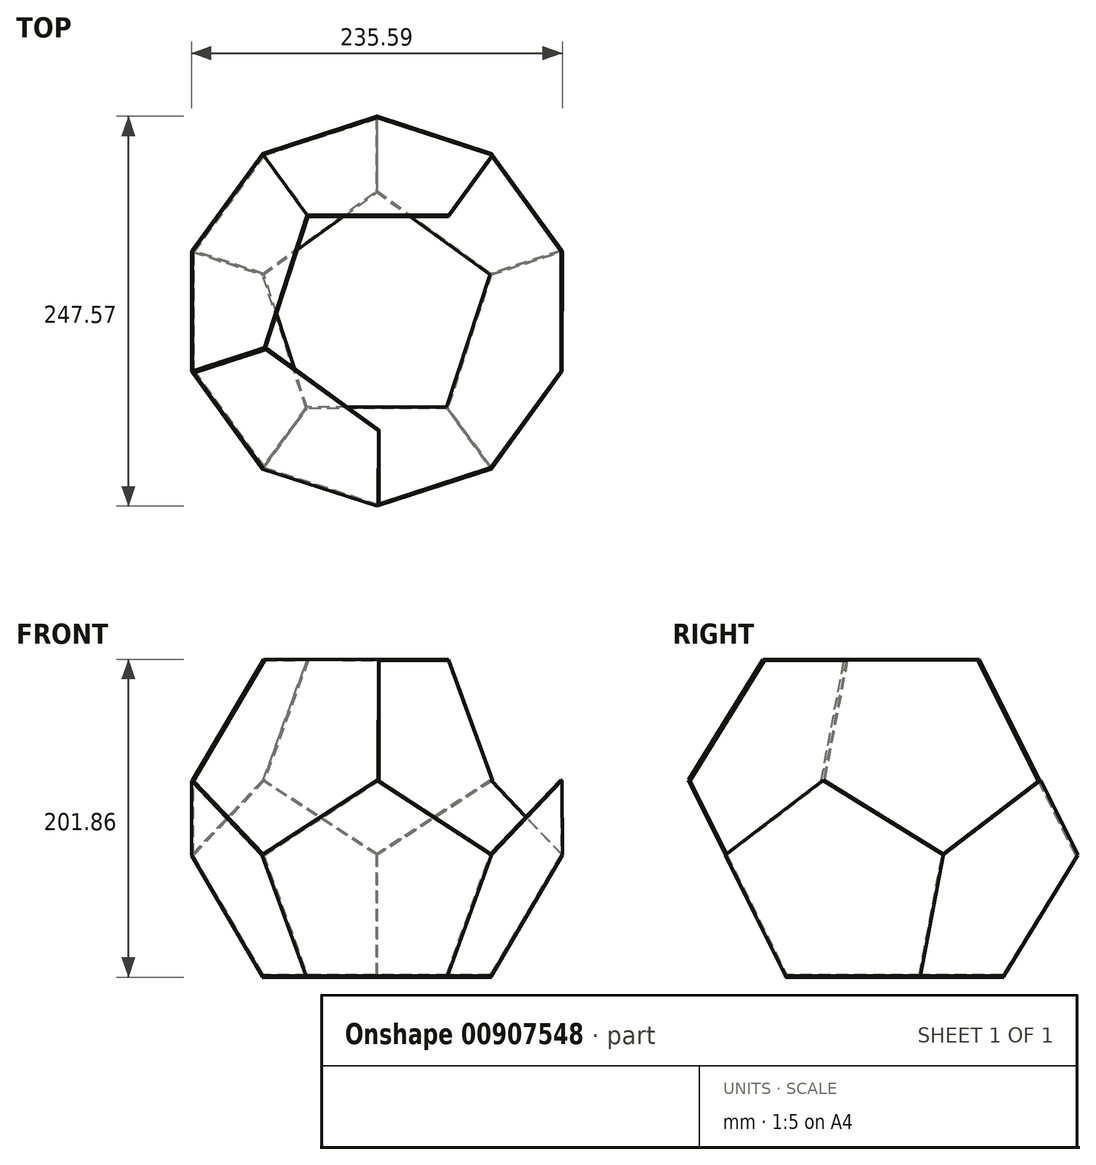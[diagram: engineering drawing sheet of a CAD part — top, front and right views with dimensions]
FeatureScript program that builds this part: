
annotation { "Feature Type Name" : "Feature", "Feature Type Description" : "" }
export const myFeature = defineFeature(function(context is Context, id is Id, definition is map)
    precondition{}
    {
        {
            var Q0;
            Q0=qCreatedBy(makeId("Top.planeOp"),FACE);
            var sketch = newSketch(context, id + "F0", { "sketchPlane" : qUnion([Q0])});
            skCircle(sketch, "E0.cCircle", {"center": v(0, 0) * mm, "radius": 61.94 * mm, "construction": true});
            skLineSegment(sketch, "E0.0", {"start": v(72.81, 23.66) * mm, "end": v(45, -61.94) * mm});
            skLineSegment(sketch, "E0.1", {"start": v(45, -61.94) * mm, "end": v(-45, -61.94) * mm});
            skLineSegment(sketch, "E0.2", {"start": v(-45, -61.94) * mm, "end": v(-72.81, 23.66) * mm});
            skLineSegment(sketch, "E0.3", {"start": v(-72.81, 23.66) * mm, "end": v(0, 76.56) * mm});
            skLineSegment(sketch, "E0.4", {"start": v(0, 76.56) * mm, "end": v(72.81, 23.66) * mm});
            skPoint(sketch, "E0.0.midPoint", {"position": v(58.9, -19.14) * mm});
            skSolve(sketch);
        }
        {
            var Q0;
            Q0=makeQuery(id+"F0.imprint","IMPRINT",FACE,{"disambiguationData":[TD([[makeQuery(id+"F0.imprint","IMPRINT",EDGE,{"derivedFrom":sQuery(id+"F0.wireOp",EDGE,"E0.0")}),-1.0]])]});
            extrude(context, id + "F1", {"entities" : qUnion([Q0]), "depth" : 1 * mm, "offsetDistance" : 25 * mm});
        }
        {
            var Q0;
            Q0=makeQuery(id+"F1.opExtrude","SWEPT_BODY",BODY,{"disambiguationData":[OSD([sQuery(id+"F0.wireOp",EDGE,"E0.0"),sQuery(id+"F0.wireOp",EDGE,"E0.1"),sQuery(id+"F0.wireOp",EDGE,"E0.2"),sQuery(id+"F0.wireOp",EDGE,"E0.3"),sQuery(id+"F0.wireOp",EDGE,"E0.4")])]});
            transform(context, id + "F2", {"entities" : qUnion([Q0]), "transformType" : TransformType.COPY});
        }
        {
            var Q0;
            Q0=makeQuery(id+"F2.opPattern","COPY",BODY,{"derivedFrom":makeQuery(id+"F1.opExtrude","SWEPT_BODY",BODY,{"disambiguationData":[OSD([sQuery(id+"F0.wireOp",EDGE,"E0.0"),sQuery(id+"F0.wireOp",EDGE,"E0.1"),sQuery(id+"F0.wireOp",EDGE,"E0.2"),sQuery(id+"F0.wireOp",EDGE,"E0.3"),sQuery(id+"F0.wireOp",EDGE,"E0.4")])]}),"instanceName":"1"});
            var Q1;
            Q1=makeQuery(id+"F1.opExtrude","CAP_EDGE",EDGE,{"disambiguationData":[OSD([sQuery(id+"F0.wireOp",EDGE,"E0.2")])],"isStart":false});
            transform(context, id + "F3", {"entities" : qUnion([Q0]), "transformType" : TransformType.ROTATION, "transformAxis" : qUnion([Q1]), "angle" : 116.57 * degree, "oppositeDirection" : true, "makeCopy" : false});
        }
        {
            var Q0;
            Q0=makeQuery(id+"F1.opExtrude","SWEPT_BODY",BODY,{"disambiguationData":[OSD([sQuery(id+"F0.wireOp",EDGE,"E0.0"),sQuery(id+"F0.wireOp",EDGE,"E0.1"),sQuery(id+"F0.wireOp",EDGE,"E0.2"),sQuery(id+"F0.wireOp",EDGE,"E0.3"),sQuery(id+"F0.wireOp",EDGE,"E0.4")])]});
            transform(context, id + "F4", {"entities" : qUnion([Q0]), "transformType" : TransformType.COPY});
        }
        {
            var Q0;
            Q0=makeQuery(id+"F4.opPattern","COPY",BODY,{"derivedFrom":makeQuery(id+"F1.opExtrude","SWEPT_BODY",BODY,{"disambiguationData":[OSD([sQuery(id+"F0.wireOp",EDGE,"E0.0"),sQuery(id+"F0.wireOp",EDGE,"E0.1"),sQuery(id+"F0.wireOp",EDGE,"E0.2"),sQuery(id+"F0.wireOp",EDGE,"E0.3"),sQuery(id+"F0.wireOp",EDGE,"E0.4")])]}),"instanceName":"1"});
            var Q1;
            Q1=makeQuery(id+"F1.opExtrude","CAP_EDGE",EDGE,{"disambiguationData":[OSD([sQuery(id+"F0.wireOp",EDGE,"E0.3")])],"isStart":false});
            transform(context, id + "F5", {"entities" : qUnion([Q0]), "transformType" : TransformType.ROTATION, "transformAxis" : qUnion([Q1]), "angle" : 116.51 * degree, "oppositeDirection" : true, "makeCopy" : false});
        }
        {
            var Q0;
            Q0=makeQuery(id+"F1.opExtrude","SWEPT_BODY",BODY,{"disambiguationData":[OSD([sQuery(id+"F0.wireOp",EDGE,"E0.0"),sQuery(id+"F0.wireOp",EDGE,"E0.1"),sQuery(id+"F0.wireOp",EDGE,"E0.2"),sQuery(id+"F0.wireOp",EDGE,"E0.3"),sQuery(id+"F0.wireOp",EDGE,"E0.4")])]});
            transform(context, id + "F6", {"entities" : qUnion([Q0]), "transformType" : TransformType.COPY});
        }
        {
            var Q0;
            Q0=makeQuery(id+"F6.opPattern","COPY",BODY,{"derivedFrom":makeQuery(id+"F1.opExtrude","SWEPT_BODY",BODY,{"disambiguationData":[OSD([sQuery(id+"F0.wireOp",EDGE,"E0.0"),sQuery(id+"F0.wireOp",EDGE,"E0.1"),sQuery(id+"F0.wireOp",EDGE,"E0.2"),sQuery(id+"F0.wireOp",EDGE,"E0.3"),sQuery(id+"F0.wireOp",EDGE,"E0.4")])]}),"instanceName":"1"});
            var Q1;
            Q1=makeQuery(id+"F1.opExtrude","CAP_EDGE",EDGE,{"disambiguationData":[OSD([sQuery(id+"F0.wireOp",EDGE,"E0.4")])],"isStart":false});
            transform(context, id + "F7", {"entities" : qUnion([Q0]), "transformType" : TransformType.ROTATION, "transformAxis" : qUnion([Q1]), "angle" : 116.51 * degree, "oppositeDirection" : true, "makeCopy" : false});
        }
        {
            var Q0;
            Q0=makeQuery(id+"F1.opExtrude","SWEPT_BODY",BODY,{"disambiguationData":[OSD([sQuery(id+"F0.wireOp",EDGE,"E0.0"),sQuery(id+"F0.wireOp",EDGE,"E0.1"),sQuery(id+"F0.wireOp",EDGE,"E0.2"),sQuery(id+"F0.wireOp",EDGE,"E0.3"),sQuery(id+"F0.wireOp",EDGE,"E0.4")])]});
            transform(context, id + "F8", {"entities" : qUnion([Q0]), "transformType" : TransformType.COPY});
        }
        {
            var Q0;
            Q0=makeQuery(id+"F8.opPattern","COPY",BODY,{"derivedFrom":makeQuery(id+"F1.opExtrude","SWEPT_BODY",BODY,{"disambiguationData":[OSD([sQuery(id+"F0.wireOp",EDGE,"E0.0"),sQuery(id+"F0.wireOp",EDGE,"E0.1"),sQuery(id+"F0.wireOp",EDGE,"E0.2"),sQuery(id+"F0.wireOp",EDGE,"E0.3"),sQuery(id+"F0.wireOp",EDGE,"E0.4")])]}),"instanceName":"1"});
            var Q1;
            Q1=makeQuery(id+"F1.opExtrude","CAP_EDGE",EDGE,{"disambiguationData":[OSD([sQuery(id+"F0.wireOp",EDGE,"E0.0")])],"isStart":false});
            transform(context, id + "F9", {"entities" : qUnion([Q0]), "transformType" : TransformType.ROTATION, "transformAxis" : qUnion([Q1]), "angle" : 116.51 * degree, "oppositeDirection" : true, "makeCopy" : false});
        }
        {
            var Q0;
            Q0=makeQuery(id+"F1.opExtrude","SWEPT_BODY",BODY,{"disambiguationData":[OSD([sQuery(id+"F0.wireOp",EDGE,"E0.0"),sQuery(id+"F0.wireOp",EDGE,"E0.1"),sQuery(id+"F0.wireOp",EDGE,"E0.2"),sQuery(id+"F0.wireOp",EDGE,"E0.3"),sQuery(id+"F0.wireOp",EDGE,"E0.4")])]});
            transform(context, id + "F10", {"entities" : qUnion([Q0]), "transformType" : TransformType.COPY});
        }
        {
            var Q0;
            Q0=makeQuery(id+"F10.opPattern","COPY",BODY,{"derivedFrom":makeQuery(id+"F1.opExtrude","SWEPT_BODY",BODY,{"disambiguationData":[OSD([sQuery(id+"F0.wireOp",EDGE,"E0.0"),sQuery(id+"F0.wireOp",EDGE,"E0.1"),sQuery(id+"F0.wireOp",EDGE,"E0.2"),sQuery(id+"F0.wireOp",EDGE,"E0.3"),sQuery(id+"F0.wireOp",EDGE,"E0.4")])]}),"instanceName":"1"});
            var Q1;
            Q1=makeQuery(id+"F1.opExtrude","CAP_EDGE",EDGE,{"disambiguationData":[OSD([sQuery(id+"F0.wireOp",EDGE,"E0.1")])],"isStart":false});
            transform(context, id + "F11", {"entities" : qUnion([Q0]), "transformType" : TransformType.ROTATION, "transformAxis" : qUnion([Q1]), "angle" : 116.51 * degree, "oppositeDirection" : true, "makeCopy" : false});
        }
        {
            var Q0;
            Q0=makeQuery(id+"F4.opPattern","COPY",BODY,{"derivedFrom":makeQuery(id+"F1.opExtrude","SWEPT_BODY",BODY,{"disambiguationData":[OSD([sQuery(id+"F0.wireOp",EDGE,"E0.0"),sQuery(id+"F0.wireOp",EDGE,"E0.1"),sQuery(id+"F0.wireOp",EDGE,"E0.2"),sQuery(id+"F0.wireOp",EDGE,"E0.3"),sQuery(id+"F0.wireOp",EDGE,"E0.4")])]}),"instanceName":"1"});
            transform(context, id + "F12", {"entities" : qUnion([Q0]), "transformType" : TransformType.COPY});
        }
        {
            var Q0;
            Q0=makeQuery(id+"F12.opPattern","COPY",BODY,{"derivedFrom":makeQuery(id+"F4.opPattern","COPY",BODY,{"derivedFrom":makeQuery(id+"F1.opExtrude","SWEPT_BODY",BODY,{"disambiguationData":[OSD([sQuery(id+"F0.wireOp",EDGE,"E0.0"),sQuery(id+"F0.wireOp",EDGE,"E0.1"),sQuery(id+"F0.wireOp",EDGE,"E0.2"),sQuery(id+"F0.wireOp",EDGE,"E0.3"),sQuery(id+"F0.wireOp",EDGE,"E0.4")])]}),"instanceName":"1"}),"instanceName":"1"});
            var Q1;
            Q1=makeQuery(id+"F4.opPattern","COPY",EDGE,{"derivedFrom":makeQuery(id+"F1.opExtrude","CAP_EDGE",EDGE,{"disambiguationData":[OSD([sQuery(id+"F0.wireOp",EDGE,"E0.0")])],"isStart":true}),"instanceName":"1"});
            transform(context, id + "F13", {"entities" : qUnion([Q0]), "transformType" : TransformType.ROTATION, "transformAxis" : qUnion([Q1]), "angle" : 116.51 * degree, "makeCopy" : false});
        }
        {
            var Q0;
            Q0=makeQuery(id+"F12.opPattern","COPY",BODY,{"derivedFrom":makeQuery(id+"F4.opPattern","COPY",BODY,{"derivedFrom":makeQuery(id+"F1.opExtrude","SWEPT_BODY",BODY,{"disambiguationData":[OSD([sQuery(id+"F0.wireOp",EDGE,"E0.0"),sQuery(id+"F0.wireOp",EDGE,"E0.1"),sQuery(id+"F0.wireOp",EDGE,"E0.2"),sQuery(id+"F0.wireOp",EDGE,"E0.3"),sQuery(id+"F0.wireOp",EDGE,"E0.4")])]}),"instanceName":"1"}),"instanceName":"1"});
            transform(context, id + "F14", {"entities" : qUnion([Q0]), "transformType" : TransformType.COPY});
        }
        {
            var Q0;
            Q0=makeQuery(id+"F14.opPattern","COPY",BODY,{"derivedFrom":makeQuery(id+"F12.opPattern","COPY",BODY,{"derivedFrom":makeQuery(id+"F4.opPattern","COPY",BODY,{"derivedFrom":makeQuery(id+"F1.opExtrude","SWEPT_BODY",BODY,{"disambiguationData":[OSD([sQuery(id+"F0.wireOp",EDGE,"E0.0"),sQuery(id+"F0.wireOp",EDGE,"E0.1"),sQuery(id+"F0.wireOp",EDGE,"E0.2"),sQuery(id+"F0.wireOp",EDGE,"E0.3"),sQuery(id+"F0.wireOp",EDGE,"E0.4")])]}),"instanceName":"1"}),"instanceName":"1"}),"instanceName":"1"});
            var Q1;
            Q1=makeQuery(id+"F12.opPattern","COPY",EDGE,{"derivedFrom":makeQuery(id+"F4.opPattern","COPY",EDGE,{"derivedFrom":makeQuery(id+"F1.opExtrude","CAP_EDGE",EDGE,{"disambiguationData":[OSD([sQuery(id+"F0.wireOp",EDGE,"E0.1")])],"isStart":false}),"instanceName":"1"}),"instanceName":"1"});
            transform(context, id + "F15", {"entities" : qUnion([Q0]), "transformType" : TransformType.ROTATION, "transformAxis" : qUnion([Q1]), "angle" : 116.51 * degree, "oppositeDirection" : true, "makeCopy" : false});
        }
        {
            var Q0;
            Q0=makeQuery(id+"F2.opPattern","COPY",BODY,{"derivedFrom":makeQuery(id+"F1.opExtrude","SWEPT_BODY",BODY,{"disambiguationData":[OSD([sQuery(id+"F0.wireOp",EDGE,"E0.0"),sQuery(id+"F0.wireOp",EDGE,"E0.1"),sQuery(id+"F0.wireOp",EDGE,"E0.2"),sQuery(id+"F0.wireOp",EDGE,"E0.3"),sQuery(id+"F0.wireOp",EDGE,"E0.4")])]}),"instanceName":"1"});
            transform(context, id + "F16", {"entities" : qUnion([Q0]), "transformType" : TransformType.COPY});
        }
        {
            var Q0;
            Q0=makeQuery(id+"F16.opPattern","COPY",BODY,{"derivedFrom":makeQuery(id+"F2.opPattern","COPY",BODY,{"derivedFrom":makeQuery(id+"F1.opExtrude","SWEPT_BODY",BODY,{"disambiguationData":[OSD([sQuery(id+"F0.wireOp",EDGE,"E0.0"),sQuery(id+"F0.wireOp",EDGE,"E0.1"),sQuery(id+"F0.wireOp",EDGE,"E0.2"),sQuery(id+"F0.wireOp",EDGE,"E0.3"),sQuery(id+"F0.wireOp",EDGE,"E0.4")])]}),"instanceName":"1"}),"instanceName":"1"});
            var Q1;
            Q1=makeQuery(id+"F2.opPattern","COPY",EDGE,{"derivedFrom":makeQuery(id+"F1.opExtrude","CAP_EDGE",EDGE,{"disambiguationData":[OSD([sQuery(id+"F0.wireOp",EDGE,"E0.0")])],"isStart":true}),"instanceName":"1"});
            transform(context, id + "F17", {"entities" : qUnion([Q0]), "transformType" : TransformType.ROTATION, "transformAxis" : qUnion([Q1]), "angle" : 116.51 * degree, "makeCopy" : false});
        }
        {
            var Q0;
            Q0=makeQuery(id+"F16.opPattern","COPY",BODY,{"derivedFrom":makeQuery(id+"F2.opPattern","COPY",BODY,{"derivedFrom":makeQuery(id+"F1.opExtrude","SWEPT_BODY",BODY,{"disambiguationData":[OSD([sQuery(id+"F0.wireOp",EDGE,"E0.0"),sQuery(id+"F0.wireOp",EDGE,"E0.1"),sQuery(id+"F0.wireOp",EDGE,"E0.2"),sQuery(id+"F0.wireOp",EDGE,"E0.3"),sQuery(id+"F0.wireOp",EDGE,"E0.4")])]}),"instanceName":"1"}),"instanceName":"1"});
            deleteBodies(context, id + "F18", {"entities" : qUnion([Q0])});
        }
        {
            var Q0;
            Q0=makeQuery(id+"F14.opPattern","COPY",BODY,{"derivedFrom":makeQuery(id+"F12.opPattern","COPY",BODY,{"derivedFrom":makeQuery(id+"F4.opPattern","COPY",BODY,{"derivedFrom":makeQuery(id+"F1.opExtrude","SWEPT_BODY",BODY,{"disambiguationData":[OSD([sQuery(id+"F0.wireOp",EDGE,"E0.0"),sQuery(id+"F0.wireOp",EDGE,"E0.1"),sQuery(id+"F0.wireOp",EDGE,"E0.2"),sQuery(id+"F0.wireOp",EDGE,"E0.3"),sQuery(id+"F0.wireOp",EDGE,"E0.4")])]}),"instanceName":"1"}),"instanceName":"1"}),"instanceName":"1"});
            deleteBodies(context, id + "F19", {"entities" : qUnion([Q0])});
        }
        {
            var Q0;
            Q0=makeQuery(id+"F4.opPattern","COPY",BODY,{"derivedFrom":makeQuery(id+"F1.opExtrude","SWEPT_BODY",BODY,{"disambiguationData":[OSD([sQuery(id+"F0.wireOp",EDGE,"E0.0"),sQuery(id+"F0.wireOp",EDGE,"E0.1"),sQuery(id+"F0.wireOp",EDGE,"E0.2"),sQuery(id+"F0.wireOp",EDGE,"E0.3"),sQuery(id+"F0.wireOp",EDGE,"E0.4")])]}),"instanceName":"1"});
            transform(context, id + "F20", {"entities" : qUnion([Q0]), "transformType" : TransformType.COPY});
        }
        {
            var Q0;
            Q0=makeQuery(id+"F20.opPattern","COPY",BODY,{"derivedFrom":makeQuery(id+"F4.opPattern","COPY",BODY,{"derivedFrom":makeQuery(id+"F1.opExtrude","SWEPT_BODY",BODY,{"disambiguationData":[OSD([sQuery(id+"F0.wireOp",EDGE,"E0.0"),sQuery(id+"F0.wireOp",EDGE,"E0.1"),sQuery(id+"F0.wireOp",EDGE,"E0.2"),sQuery(id+"F0.wireOp",EDGE,"E0.3"),sQuery(id+"F0.wireOp",EDGE,"E0.4")])]}),"instanceName":"1"}),"instanceName":"1"});
            var Q1;
            Q1=makeQuery(id+"F4.opPattern","COPY",EDGE,{"derivedFrom":makeQuery(id+"F1.opExtrude","CAP_EDGE",EDGE,{"disambiguationData":[OSD([sQuery(id+"F0.wireOp",EDGE,"E0.1")])],"isStart":true}),"instanceName":"1"});
            transform(context, id + "F21", {"entities" : qUnion([Q0]), "transformType" : TransformType.ROTATION, "transformAxis" : qUnion([Q1]), "angle" : 116.51 * degree, "makeCopy" : false});
        }
        {
            var Q0;
            Q0=makeQuery(id+"F2.opPattern","COPY",BODY,{"derivedFrom":makeQuery(id+"F1.opExtrude","SWEPT_BODY",BODY,{"disambiguationData":[OSD([sQuery(id+"F0.wireOp",EDGE,"E0.0"),sQuery(id+"F0.wireOp",EDGE,"E0.1"),sQuery(id+"F0.wireOp",EDGE,"E0.2"),sQuery(id+"F0.wireOp",EDGE,"E0.3"),sQuery(id+"F0.wireOp",EDGE,"E0.4")])]}),"instanceName":"1"});
            transform(context, id + "F22", {"entities" : qUnion([Q0]), "transformType" : TransformType.COPY});
        }
        {
            var Q0;
            Q0=makeQuery(id+"F22.opPattern","COPY",BODY,{"derivedFrom":makeQuery(id+"F2.opPattern","COPY",BODY,{"derivedFrom":makeQuery(id+"F1.opExtrude","SWEPT_BODY",BODY,{"disambiguationData":[OSD([sQuery(id+"F0.wireOp",EDGE,"E0.0"),sQuery(id+"F0.wireOp",EDGE,"E0.1"),sQuery(id+"F0.wireOp",EDGE,"E0.2"),sQuery(id+"F0.wireOp",EDGE,"E0.3"),sQuery(id+"F0.wireOp",EDGE,"E0.4")])]}),"instanceName":"1"}),"instanceName":"1"});
            var Q1;
            Q1=makeQuery(id+"F2.opPattern","COPY",EDGE,{"derivedFrom":makeQuery(id+"F1.opExtrude","CAP_EDGE",EDGE,{"disambiguationData":[OSD([sQuery(id+"F0.wireOp",EDGE,"E0.0")])],"isStart":true}),"instanceName":"1"});
            transform(context, id + "F23", {"entities" : qUnion([Q0]), "transformType" : TransformType.ROTATION, "transformAxis" : qUnion([Q1]), "angle" : 116.51 * degree, "makeCopy" : false});
        }
        {
            var Q0;
            Q0=makeQuery(id+"F20.opPattern","COPY",BODY,{"derivedFrom":makeQuery(id+"F4.opPattern","COPY",BODY,{"derivedFrom":makeQuery(id+"F1.opExtrude","SWEPT_BODY",BODY,{"disambiguationData":[OSD([sQuery(id+"F0.wireOp",EDGE,"E0.0"),sQuery(id+"F0.wireOp",EDGE,"E0.1"),sQuery(id+"F0.wireOp",EDGE,"E0.2"),sQuery(id+"F0.wireOp",EDGE,"E0.3"),sQuery(id+"F0.wireOp",EDGE,"E0.4")])]}),"instanceName":"1"}),"instanceName":"1"});
            transform(context, id + "F24", {"entities" : qUnion([Q0]), "transformType" : TransformType.COPY});
        }
    });
